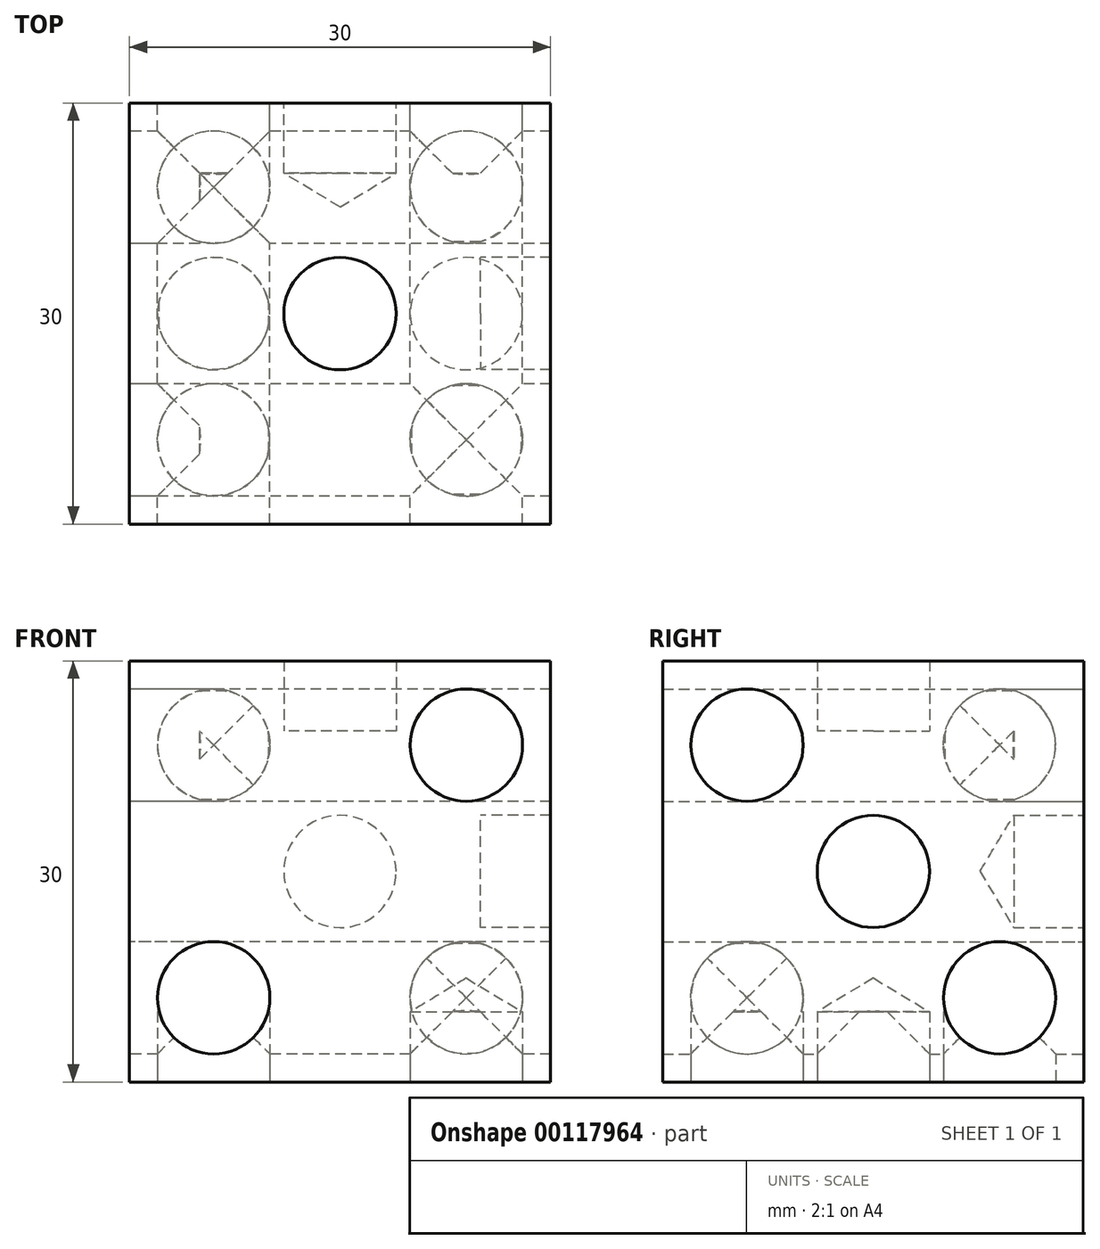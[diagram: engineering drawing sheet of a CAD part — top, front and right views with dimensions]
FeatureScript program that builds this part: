
annotation { "Feature Type Name" : "Feature", "Feature Type Description" : "" }
export const myFeature = defineFeature(function(context is Context, id is Id, definition is map)
    precondition{}
    {
        {
            var Q0;
            Q0=qCreatedBy(makeId("Top.planeOp"),FACE);
            var sketch = newSketch(context, id + "F0", { "sketchPlane" : qUnion([Q0])});
            skLineSegment(sketch, "E0.bottom", {"start": v(0, 0) * mm, "end": v(30, 0) * mm});
            skLineSegment(sketch, "E0.top", {"start": v(0, -30) * mm, "end": v(30, -30) * mm});
            skLineSegment(sketch, "E0.left", {"start": v(0, 0) * mm, "end": v(0, -30) * mm});
            skLineSegment(sketch, "E0.right", {"start": v(30, 0) * mm, "end": v(30, -30) * mm});
            skCircle(sketch, "E1", {"center": v(6, -6) * mm, "radius": 4 * mm});
            skCircle(sketch, "E2", {"center": v(6, -15) * mm, "radius": 4 * mm});
            skCircle(sketch, "E3", {"center": v(6, -24) * mm, "radius": 4 * mm});
            skCircle(sketch, "E4", {"center": v(24, -6) * mm, "radius": 4 * mm});
            skCircle(sketch, "E5", {"center": v(24, -15) * mm, "radius": 4 * mm});
            skCircle(sketch, "E6", {"center": v(24, -24) * mm, "radius": 4 * mm});
            skCircle(sketch, "E7", {"center": v(15, -15) * mm, "radius": 4 * mm});
            skSolve(sketch);
        }
        {
            var Q0;
            Q0=qCreatedBy(makeId("Right.planeOp"),FACE);
            var sketch = newSketch(context, id + "F1", { "sketchPlane" : qUnion([Q0])});
            skLineSegment(sketch, "E8.bottom", {"start": v(0, 0) * mm, "end": v(-30, 0) * mm});
            skLineSegment(sketch, "E8.top", {"start": v(0, 30) * mm, "end": v(-30, 30) * mm});
            skLineSegment(sketch, "E8.left", {"start": v(0, 0) * mm, "end": v(0, 30) * mm});
            skLineSegment(sketch, "E8.right", {"start": v(-30, 0) * mm, "end": v(-30, 30) * mm});
            skCircle(sketch, "E9", {"center": v(-24, 24) * mm, "radius": 4 * mm});
            skCircle(sketch, "E10", {"center": v(-15, 15) * mm, "radius": 4 * mm});
            skCircle(sketch, "E11", {"center": v(-6, 6) * mm, "radius": 4 * mm});
            skCircle(sketch, "E12", {"center": v(-24, 6) * mm, "radius": 4 * mm});
            skCircle(sketch, "E13", {"center": v(-6, 24) * mm, "radius": 4 * mm});
            skSolve(sketch);
        }
        {
            var Q0;
            Q0=qCreatedBy(makeId("Front.planeOp"),FACE);
            var sketch = newSketch(context, id + "F2", { "sketchPlane" : qUnion([Q0])});
            skLineSegment(sketch, "E14.bottom", {"start": v(0, 30) * mm, "end": v(30, 30) * mm});
            skLineSegment(sketch, "E14.top", {"start": v(0, 0) * mm, "end": v(30, 0) * mm});
            skLineSegment(sketch, "E14.left", {"start": v(0, 30) * mm, "end": v(0, 0) * mm});
            skLineSegment(sketch, "E14.right", {"start": v(30, 30) * mm, "end": v(30, 0) * mm});
            skCircle(sketch, "E15", {"center": v(6, 24) * mm, "radius": 4 * mm});
            skCircle(sketch, "E16", {"center": v(6, 6) * mm, "radius": 4 * mm});
            skCircle(sketch, "E17", {"center": v(24, 24) * mm, "radius": 4 * mm});
            skCircle(sketch, "E18", {"center": v(24, 6) * mm, "radius": 4 * mm});
            skCircle(sketch, "E19", {"center": v(15, 15) * mm, "radius": 4 * mm});
            skSolve(sketch);
        }
        {
            var Q0;
            Q0=makeQuery(id+"F2.imprint","IMPRINT",FACE,{"disambiguationData":[TD([[makeQuery(id+"F2.imprint","IMPRINT",EDGE,{"derivedFrom":sQuery(id+"F2.wireOp",EDGE,"E14.bottom")}),-1.0]])]});
            extrude(context, id + "F3", {"entities" : qUnion([Q0]), "depth" : 30 * mm});
        }
        {
            var Q0;
            Q0=makeQuery(id+"F1.imprint","IMPRINT",FACE,{"disambiguationData":[TD([[makeQuery(id+"F1.imprint","IMPRINT",EDGE,{"derivedFrom":sQuery(id+"F1.wireOp",EDGE,"E8.bottom")}),-1.0]])]});
            extrude(context, id + "F4", {"entities" : qUnion([Q0]), "operationType" : NewBodyOperationType.ADD, "depth" : 30 * mm});
        }
        {
            var Q0;
            Q0=makeQuery(id+"F0.imprint","IMPRINT",FACE,{"disambiguationData":[TD([[makeQuery(id+"F0.imprint","IMPRINT",EDGE,{"derivedFrom":sQuery(id+"F0.wireOp",EDGE,"E0.bottom")}),-1.0]])]});
            extrude(context, id + "F5", {"entities" : qUnion([Q0]), "operationType" : NewBodyOperationType.ADD, "depth" : 30 * mm});
        }
        {
            var Q0;
            Q0=makeQuery(id+"F2.imprint","IMPRINT",FACE,{"disambiguationData":[TD([[makeQuery(id+"F2.imprint","IMPRINT",EDGE,{"derivedFrom":sQuery(id+"F2.wireOp",EDGE,"E17")}),1.0]])]});
            extrude(context, id + "F6", {"entities" : qUnion([Q0]), "operationType" : NewBodyOperationType.ADD, "depth" : 30 * mm});
        }
        {
            var Q0;
            Q0=sQuery(id+"F2.wireOp",VERTEX,"E17.center");
            var Q1;
            Q1=makeQuery(id+"F3.opExtrude","SWEPT_BODY",BODY,{"disambiguationData":[OSD([sQuery(id+"F2.wireOp",EDGE,"E14.bottom"),sQuery(id+"F2.wireOp",EDGE,"E14.top"),sQuery(id+"F2.wireOp",EDGE,"E14.left"),sQuery(id+"F2.wireOp",EDGE,"E14.right"),sQuery(id+"F2.wireOp",EDGE,"E15"),sQuery(id+"F2.wireOp",EDGE,"E16"),sQuery(id+"F2.wireOp",EDGE,"E17"),sQuery(id+"F2.wireOp",EDGE,"E18"),sQuery(id+"F2.wireOp",EDGE,"E19")])]});
            hole(context, id + "F7", {"style" : HoleStyle.SIMPLE, "endStyle" : HoleEndStyle.BLIND, "oppositeDirection" : true, "holeDiameter" : 8 * mm, "holeDepth" : 30 * mm, "locations" : qUnion([Q0]), "scope" : qUnion([Q1])});
        }
        {
            var Q0;
            Q0=sQuery(id+"F2.wireOp",VERTEX,"E16.center");
            var Q1;
            Q1=makeQuery(id+"F3.opExtrude","SWEPT_BODY",BODY,{"disambiguationData":[OSD([sQuery(id+"F2.wireOp",EDGE,"E14.bottom"),sQuery(id+"F2.wireOp",EDGE,"E14.top"),sQuery(id+"F2.wireOp",EDGE,"E14.left"),sQuery(id+"F2.wireOp",EDGE,"E14.right"),sQuery(id+"F2.wireOp",EDGE,"E15"),sQuery(id+"F2.wireOp",EDGE,"E16"),sQuery(id+"F2.wireOp",EDGE,"E17"),sQuery(id+"F2.wireOp",EDGE,"E18"),sQuery(id+"F2.wireOp",EDGE,"E19")])]});
            hole(context, id + "F8", {"style" : HoleStyle.SIMPLE, "endStyle" : HoleEndStyle.BLIND, "oppositeDirection" : true, "holeDiameter" : 8 * mm, "holeDepth" : 30 * mm, "locations" : qUnion([Q0]), "scope" : qUnion([Q1])});
        }
        {
            var Q0;
            Q0=sQuery(id+"F2.wireOp",VERTEX,"E15.center");
            var Q1;
            Q1=makeQuery(id+"F3.opExtrude","SWEPT_BODY",BODY,{"disambiguationData":[OSD([sQuery(id+"F2.wireOp",EDGE,"E14.bottom"),sQuery(id+"F2.wireOp",EDGE,"E14.top"),sQuery(id+"F2.wireOp",EDGE,"E14.left"),sQuery(id+"F2.wireOp",EDGE,"E14.right"),sQuery(id+"F2.wireOp",EDGE,"E15"),sQuery(id+"F2.wireOp",EDGE,"E16"),sQuery(id+"F2.wireOp",EDGE,"E17"),sQuery(id+"F2.wireOp",EDGE,"E18"),sQuery(id+"F2.wireOp",EDGE,"E19")])]});
            hole(context, id + "F9", {"style" : HoleStyle.SIMPLE, "endStyle" : HoleEndStyle.BLIND, "oppositeDirection" : true, "holeDiameter" : 8 * mm, "holeDepth" : 5 * mm, "locations" : qUnion([Q0]), "scope" : qUnion([Q1])});
        }
        {
            var Q0;
            Q0=sQuery(id+"F2.wireOp",VERTEX,"E19.center");
            var Q1;
            Q1=makeQuery(id+"F3.opExtrude","SWEPT_BODY",BODY,{"disambiguationData":[OSD([sQuery(id+"F2.wireOp",EDGE,"E14.bottom"),sQuery(id+"F2.wireOp",EDGE,"E14.top"),sQuery(id+"F2.wireOp",EDGE,"E14.left"),sQuery(id+"F2.wireOp",EDGE,"E14.right"),sQuery(id+"F2.wireOp",EDGE,"E15"),sQuery(id+"F2.wireOp",EDGE,"E16"),sQuery(id+"F2.wireOp",EDGE,"E17"),sQuery(id+"F2.wireOp",EDGE,"E18"),sQuery(id+"F2.wireOp",EDGE,"E19")])]});
            hole(context, id + "F10", {"style" : HoleStyle.SIMPLE, "endStyle" : HoleEndStyle.BLIND, "oppositeDirection" : true, "holeDiameter" : 8 * mm, "holeDepth" : 5 * mm, "locations" : qUnion([Q0]), "scope" : qUnion([Q1])});
        }
        {
            var Q0;
            Q0=sQuery(id+"F2.wireOp",VERTEX,"E18.center");
            var Q1;
            Q1=makeQuery(id+"F3.opExtrude","SWEPT_BODY",BODY,{"disambiguationData":[OSD([sQuery(id+"F2.wireOp",EDGE,"E14.bottom"),sQuery(id+"F2.wireOp",EDGE,"E14.top"),sQuery(id+"F2.wireOp",EDGE,"E14.left"),sQuery(id+"F2.wireOp",EDGE,"E14.right"),sQuery(id+"F2.wireOp",EDGE,"E15"),sQuery(id+"F2.wireOp",EDGE,"E16"),sQuery(id+"F2.wireOp",EDGE,"E17"),sQuery(id+"F2.wireOp",EDGE,"E18"),sQuery(id+"F2.wireOp",EDGE,"E19")])]});
            hole(context, id + "F11", {"style" : HoleStyle.SIMPLE, "endStyle" : HoleEndStyle.BLIND, "oppositeDirection" : true, "holeDiameter" : 8 * mm, "holeDepth" : 5 * mm, "locations" : qUnion([Q0]), "scope" : qUnion([Q1])});
        }
        {
            var Q0;
            Q0=sQuery(id+"F0.wireOp",VERTEX,"E3.center");
            var Q1;
            Q1=sQuery(id+"F0.wireOp",VERTEX,"E2.center");
            var Q2;
            Q2=sQuery(id+"F0.wireOp",VERTEX,"E1.center");
            var Q3;
            Q3=sQuery(id+"F0.wireOp",VERTEX,"E4.center");
            var Q4;
            Q4=sQuery(id+"F0.wireOp",VERTEX,"E5.center");
            var Q5;
            Q5=sQuery(id+"F0.wireOp",VERTEX,"E6.center");
            var Q6;
            Q6=makeQuery(id+"F3.opExtrude","SWEPT_BODY",BODY,{"disambiguationData":[OSD([sQuery(id+"F2.wireOp",EDGE,"E14.bottom"),sQuery(id+"F2.wireOp",EDGE,"E14.top"),sQuery(id+"F2.wireOp",EDGE,"E14.left"),sQuery(id+"F2.wireOp",EDGE,"E14.right"),sQuery(id+"F2.wireOp",EDGE,"E15"),sQuery(id+"F2.wireOp",EDGE,"E16"),sQuery(id+"F2.wireOp",EDGE,"E17"),sQuery(id+"F2.wireOp",EDGE,"E18"),sQuery(id+"F2.wireOp",EDGE,"E19")])]});
            hole(context, id + "F12", {"style" : HoleStyle.SIMPLE, "endStyle" : HoleEndStyle.BLIND, "oppositeDirection" : true, "holeDiameter" : 8 * mm, "holeDepth" : 5 * mm, "locations" : qUnion([Q0, Q1, Q2, Q3, Q4, Q5]), "scope" : qUnion([Q6])});
        }
        {
            var Q0;
            Q0=sQuery(id+"F0.wireOp",VERTEX,"E7.center");
            var Q1;
            Q1=makeQuery(id+"F3.opExtrude","SWEPT_BODY",BODY,{"disambiguationData":[OSD([sQuery(id+"F2.wireOp",EDGE,"E14.bottom"),sQuery(id+"F2.wireOp",EDGE,"E14.top"),sQuery(id+"F2.wireOp",EDGE,"E14.left"),sQuery(id+"F2.wireOp",EDGE,"E14.right"),sQuery(id+"F2.wireOp",EDGE,"E15"),sQuery(id+"F2.wireOp",EDGE,"E16"),sQuery(id+"F2.wireOp",EDGE,"E17"),sQuery(id+"F2.wireOp",EDGE,"E18"),sQuery(id+"F2.wireOp",EDGE,"E19")])]});
            hole(context, id + "F13", {"style" : HoleStyle.SIMPLE, "endStyle" : HoleEndStyle.BLIND, "oppositeDirection" : true, "holeDiameter" : 8 * mm, "holeDepth" : 30 * mm, "locations" : qUnion([Q0]), "scope" : qUnion([Q1])});
        }
        {
            var Q0;
            Q0=makeQuery(id+"F0.imprint","IMPRINT",FACE,{"disambiguationData":[TD([[makeQuery(id+"F0.imprint","IMPRINT",EDGE,{"derivedFrom":sQuery(id+"F0.wireOp",EDGE,"E7")}),1.0]])]});
            extrude(context, id + "F14", {"entities" : qUnion([Q0]), "operationType" : NewBodyOperationType.ADD, "depth" : 25 * mm});
        }
        {
            var Q0;
            Q0=sQuery(id+"F1.wireOp",VERTEX,"E9.center");
            var Q1;
            Q1=sQuery(id+"F1.wireOp",VERTEX,"E10.center");
            var Q2;
            Q2=sQuery(id+"F1.wireOp",VERTEX,"E11.center");
            var Q3;
            Q3=makeQuery(id+"F3.opExtrude","SWEPT_BODY",BODY,{"disambiguationData":[OSD([sQuery(id+"F2.wireOp",EDGE,"E14.bottom"),sQuery(id+"F2.wireOp",EDGE,"E14.top"),sQuery(id+"F2.wireOp",EDGE,"E14.left"),sQuery(id+"F2.wireOp",EDGE,"E14.right"),sQuery(id+"F2.wireOp",EDGE,"E15"),sQuery(id+"F2.wireOp",EDGE,"E16"),sQuery(id+"F2.wireOp",EDGE,"E17"),sQuery(id+"F2.wireOp",EDGE,"E18"),sQuery(id+"F2.wireOp",EDGE,"E19")])]});
            hole(context, id + "F15", {"style" : HoleStyle.SIMPLE, "endStyle" : HoleEndStyle.BLIND, "oppositeDirection" : true, "holeDiameter" : 8 * mm, "holeDepth" : 30 * mm, "locations" : qUnion([Q0, Q1, Q2]), "scope" : qUnion([Q3])});
        }
        {
            var Q0;
            Q0=sQuery(id+"F1.wireOp",VERTEX,"E13.center");
            var Q1;
            Q1=sQuery(id+"F1.wireOp",VERTEX,"E12.center");
            var Q2;
            Q2=makeQuery(id+"F3.opExtrude","SWEPT_BODY",BODY,{"disambiguationData":[OSD([sQuery(id+"F2.wireOp",EDGE,"E14.bottom"),sQuery(id+"F2.wireOp",EDGE,"E14.top"),sQuery(id+"F2.wireOp",EDGE,"E14.left"),sQuery(id+"F2.wireOp",EDGE,"E14.right"),sQuery(id+"F2.wireOp",EDGE,"E15"),sQuery(id+"F2.wireOp",EDGE,"E16"),sQuery(id+"F2.wireOp",EDGE,"E17"),sQuery(id+"F2.wireOp",EDGE,"E18"),sQuery(id+"F2.wireOp",EDGE,"E19")])]});
            hole(context, id + "F16", {"style" : HoleStyle.SIMPLE, "endStyle" : HoleEndStyle.BLIND, "oppositeDirection" : true, "holeDiameter" : 8 * mm, "holeDepth" : 5 * mm, "locations" : qUnion([Q0, Q1]), "scope" : qUnion([Q2])});
        }
        {
            var Q0;
            Q0=makeQuery(id+"F1.imprint","IMPRINT",FACE,{"disambiguationData":[TD([[makeQuery(id+"F1.imprint","IMPRINT",EDGE,{"derivedFrom":sQuery(id+"F1.wireOp",EDGE,"E10")}),1.0]])]});
            extrude(context, id + "F17", {"entities" : qUnion([Q0]), "operationType" : NewBodyOperationType.ADD, "depth" : 25 * mm});
        }
    });
